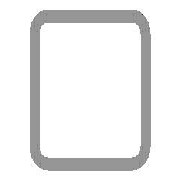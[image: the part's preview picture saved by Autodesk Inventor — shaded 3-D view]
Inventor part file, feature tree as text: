
AUTODESK INVENTOR PART (.ipt)
format: ipt  version: 2025.1 (Build 291241020, 241B)  size: 131,584 bytes
history: native  units: mm (DEFAULTED — no unit token found)
features: other x4, sketch x1, plane x1
ambient origin geometry x8: Origin, YZ Plane, XZ Plane, XY Plane, X Axis, Y Axis, Z Axis, Center Point
bodies: Solid1 (feature_tree), Body (feature_tree)
feature tree (6):
  parser-record x1  (decoder bookkeeping rows leaked as tree rows — omitted from the tree; the rows remain in map.json)
  other  "Driven Length"
  other  "Start Plane"
  other  "End Plane"
  sketch  "Sketch3"  dims[d3=1755.0mm d4=0.0mm d7=6.0mm d9=80.0mm d11=80.0mm d12=3.0mm d13=-0.0mm d14=1755.0mm d15=40.0mm d16=40.0mm d17=90.0deg d18=1755.0mm]
  plane  "Work Plane3"
